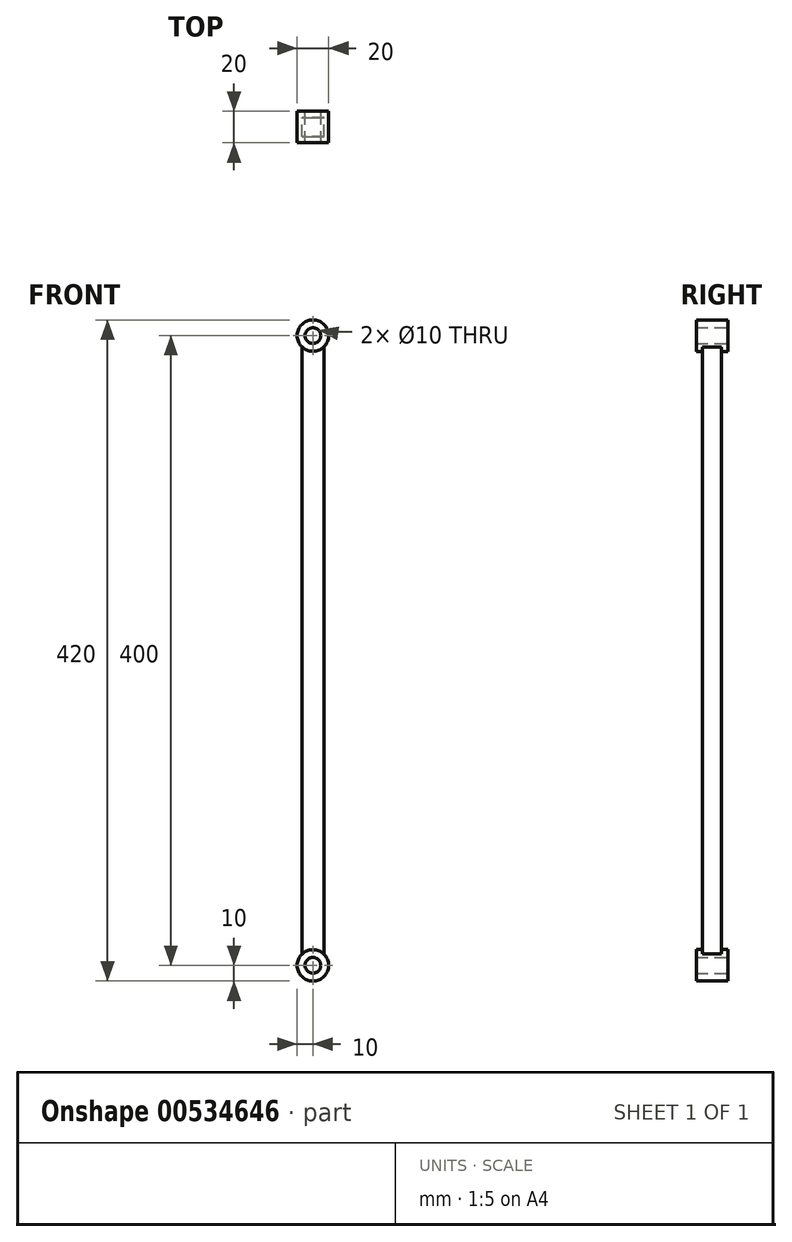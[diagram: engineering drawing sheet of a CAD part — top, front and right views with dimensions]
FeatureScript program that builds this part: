
annotation { "Feature Type Name" : "Feature", "Feature Type Description" : "" }
export const myFeature = defineFeature(function(context is Context, id is Id, definition is map)
    precondition{}
    {
        {
            var Q0;
            Q0=qCreatedBy(makeId("Front.planeOp"),FACE);
            var sketch = newSketch(context, id + "F0", { "sketchPlane" : qUnion([Q0])});
            skCircle(sketch, "E0", {"center": v(0, 200) * mm, "radius": 5 * mm});
            skCircle(sketch, "E1", {"center": v(0, 200) * mm, "radius": 10 * mm});
            skCircle(sketch, "E2", {"center": v(0, -200) * mm, "radius": 5 * mm});
            skCircle(sketch, "E3", {"center": v(0, -200) * mm, "radius": 10 * mm});
            skLineSegment(sketch, "E4", {"start": v(-7, 192.86) * mm, "end": v(-7, -192.86) * mm});
            skLineSegment(sketch, "E5", {"start": v(7, 192.86) * mm, "end": v(7, -192.86) * mm});
            skSolve(sketch);
        }
        {
            var Q0;
            Q0=makeQuery(id+"F0.imprint","IMPRINT",FACE,{"disambiguationData":[TD([[makeQuery(id+"F0.imprint","IMPRINT",EDGE,{"derivedFrom":sQuery(id+"F0.wireOp",EDGE,"E0")}),-1.0]])]});
            var Q1;
            Q1=makeQuery(id+"F0.imprint","IMPRINT",FACE,{"disambiguationData":[TD([[makeQuery(id+"F0.imprint","IMPRINT",EDGE,{"derivedFrom":sQuery(id+"F0.wireOp",EDGE,"E2")}),-1.0]])]});
            extrude(context, id + "F1", {"entities" : qUnion([Q0, Q1]), "endBound" : BoundingType.SYMMETRIC, "depth" : 20 * mm, "offsetDistance" : 25 * mm});
        }
        {
            var Q0;
            {var subQ0=sQuery(id+"F0.wireOp",EDGE,"E4");Q0=makeQuery(id+"F0.imprint","IMPRINT",FACE,{"disambiguationData":[TD([[makeQuery(id+"F0.imprint","IMPRINT",EDGE,{"derivedFrom":subQ0}),1.0]])]});}
            extrude(context, id + "F2", {"entities" : qUnion([Q0]), "operationType" : NewBodyOperationType.ADD, "endBound" : BoundingType.SYMMETRIC, "depth" : 12 * mm, "offsetDistance" : 25 * mm});
        }
    });
